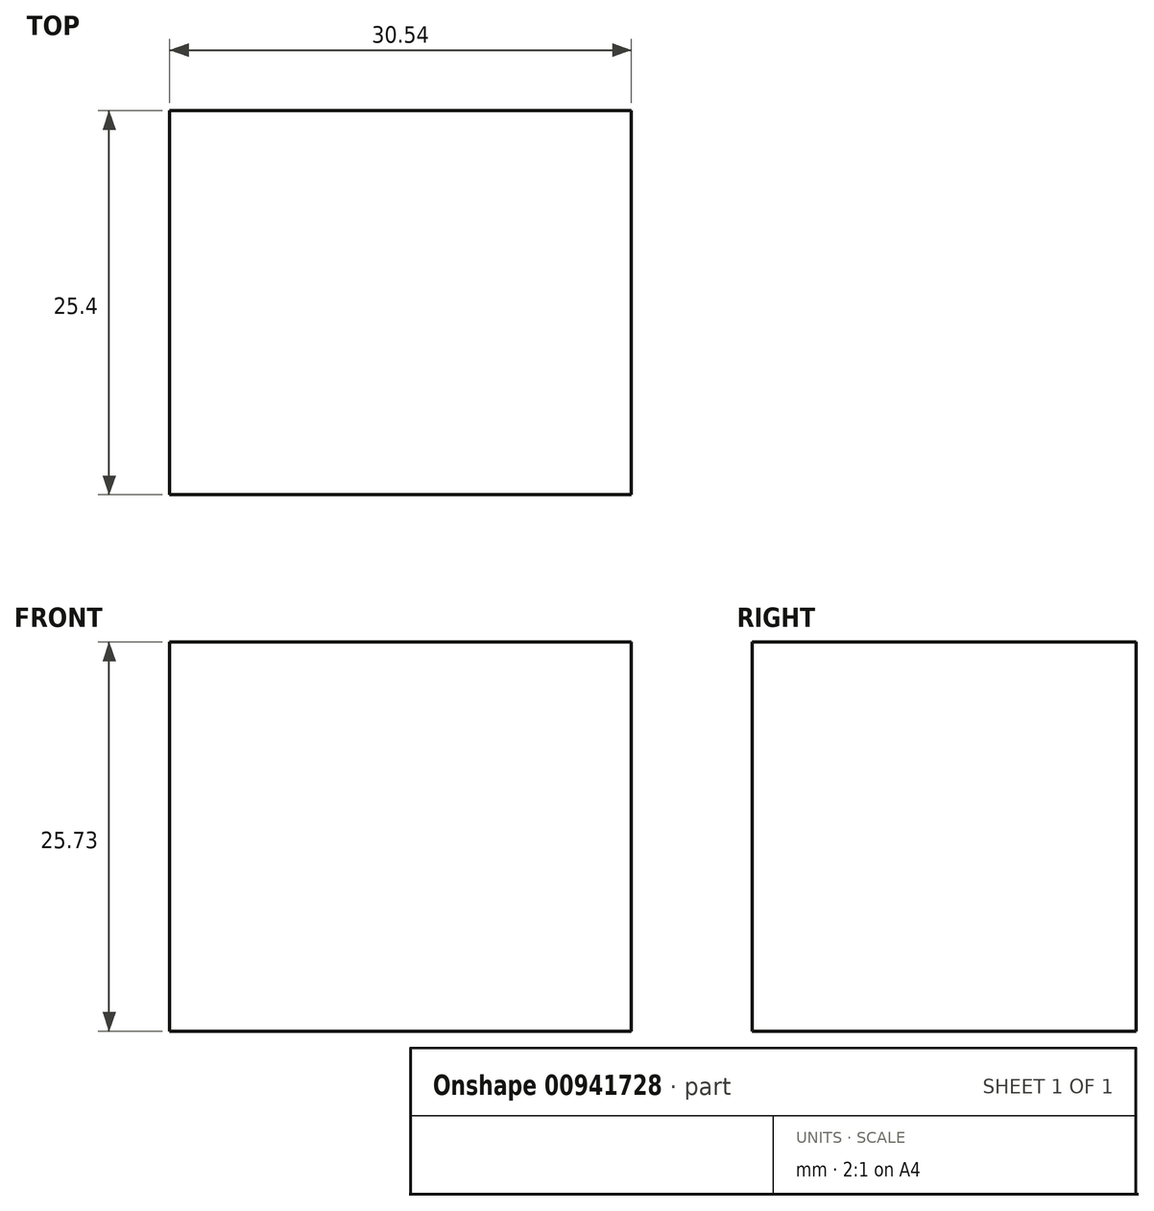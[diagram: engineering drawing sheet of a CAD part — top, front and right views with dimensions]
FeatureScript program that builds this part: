
annotation { "Feature Type Name" : "Feature", "Feature Type Description" : "" }
export const myFeature = defineFeature(function(context is Context, id is Id, definition is map)
    precondition{}
    {
        {
            var Q0;
            Q0=qCreatedBy(makeId("Front.planeOp"),FACE);
            var sketch = newSketch(context, id + "F0", { "sketchPlane" : qUnion([Q0])});
            skLineSegment(sketch, "E0.bottom", {"start": v(-17.51, -5.23) * mm, "end": v(13.03, -5.23) * mm});
            skLineSegment(sketch, "E0.top", {"start": v(-17.51, -30.96) * mm, "end": v(13.03, -30.96) * mm});
            skLineSegment(sketch, "E0.left", {"start": v(-17.51, -5.23) * mm, "end": v(-17.51, -30.96) * mm});
            skLineSegment(sketch, "E0.right", {"start": v(13.03, -5.23) * mm, "end": v(13.03, -30.96) * mm});
            skSolve(sketch);
        }
        {
            var Q0;
            Q0 = qSketchRegion(id + "F0", true);
            extrude(context, id + "F1", {"entities" : qUnion([Q0]), "depth" : 25.4 * mm, "offsetDistance" : 25.4 * mm});
        }
    });
